FCSTD DOCUMENT  (FreeCAD 1.0RUnknown)
Label: wardrobe_drawer_jan_assy4
License: All rights reserved
objects: App::Link×7, App::DocumentObjectGroup×4, PartDesign::CoordinateSystem×1, App::FeaturePython×1, App::Part×1
note: 1 computed .brp shape members not serialized (recipe doc carries the construction recipe); baked Part::Feature solids carry a one-line shape summary decoded from their .brp
EXTERNAL_REF file=../purchased parts/hettich_rail_550mm.FCStd obj=LCS_left_center
EXTERNAL_REF file=../purchased parts/hettich_rail_550mm.FCStd obj=Body
EXTERNAL_REF file=parts/drawer_sides.FCStd obj=LCS_bottom_center
EXTERNAL_REF file=../purchased parts/hettich_rail_550mm.FCStd obj=LCS_inner_center
EXTERNAL_REF file=parts/drawer_sides.FCStd obj=Body
EXTERNAL_REF file=parts/drawer_front.FCStd obj=LCS_left
EXTERNAL_REF file=parts/drawer_sides.FCStd obj=LCS_1
EXTERNAL_REF file=parts/drawer_front.FCStd obj=Body
EXTERNAL_REF file=parts/drawer_front.FCStd obj=LCS_right
EXTERNAL_REF file=parts/drawer_sides.FCStd obj=LCS_2
EXTERNAL_REF file=parts/drawer_bottom.FCStd obj=LCS_front
EXTERNAL_REF file=parts/drawer_front.FCStd obj=LCS_bottom_center
EXTERNAL_REF file=parts/drawer_bottom.FCStd obj=Body
EXTERNAL_REF file=parts/drawer_back.FCStd obj=LCS_left
EXTERNAL_REF file=parts/drawer_back.FCStd obj=Body

FEATURE [App::DocumentObjectGroup] Parts
FEATURE [PartDesign::CoordinateSystem] LCS_Origin
  AttacherType = Attacher::AttachEngine3D
  AttachmentSupport = -> [X_Axis]
  MapMode = 2
FEATURE [App::DocumentObjectGroup] Constraints
FEATURE [App::FeaturePython] Variables  # WARN: FeaturePython — macro-defined, semantics opaque (R4)
  Type = App::PropertyContainer
FEATURE [App::DocumentObjectGroup] Configurations
FEATURE [App::Link] hettich_rail_550
  AttachedBy = #LCS_left_center
  AttachedTo = Parent Assembly#LCS_Origin
  LinkPlacement = pos=(17.5,-9e-16,-1.6e-14) rot=(-0.57735,-0.57735,-0.57735;2.0944rad)
  LinkedObject = -> <external ../purchased parts/hettich_rail_550mm.FCStd>#Body
  Placement = pos=(17.5,-9e-16,-1.6e-14) rot=(-0.57735,-0.57735,-0.57735;2.0944rad)
  SolverId = Asm4EE
  expr: Placement = LCS_Origin.Placement * AttachmentOffset * hettich_rail_550mm#LCS_left_center.Placement ^ -1
FEATURE [App::Link] drawer_sides
  AttachedBy = #LCS_bottom_center
  AttachedTo = hettich_rail_550#LCS_inner_center
  AttachmentOffset = pos=(0,0,0) rot=(0,0,1;4.71239rad)
  LinkPlacement = pos=(90,22,256) rot=(0.57735,0.57735,0.57735;2.0944rad)
  LinkedObject = -> <external parts/drawer_sides.FCStd>#Body
  Placement = pos=(90,22,256) rot=(0.57735,0.57735,0.57735;2.0944rad)
  SolverId = Asm4EE
  expr: Placement = hettich_rail_550.Placement * hettich_rail_550mm#LCS_inner_center.Placement * AttachmentOffset * drawer_sides#LCS_bottom_center.Placement ^ -1
FEATURE [App::Link] drawer_front
  AttachedBy = #LCS_left
  AttachedTo = drawer_sides#LCS_1
  AttachmentOffset = pos=(0,0,0) rot=(0.707107,-0.707107,0;3.14159rad)
  LinkPlacement = pos=(90,12.5,-265.5) rot=(-0.707107,0,-0.707107;3.14159rad)
  LinkedObject = -> <external parts/drawer_front.FCStd>#Body
  Placement = pos=(90,12.5,-265.5) rot=(-0.707107,0,-0.707107;3.14159rad)
  SolverId = Asm4EE
  expr: Placement = drawer_sides.Placement * drawer_sides#LCS_1.Placement * AttachmentOffset * drawer_front#LCS_left.Placement ^ -1
FEATURE [App::Link] drawer_sides001
  AttachedBy = #LCS_2
  AttachedTo = drawer_front#LCS_right
  AttachmentOffset = pos=(0,0,0) rot=(0.707107,0.707107,0;3.14159rad)
  LinkPlacement = pos=(90,480,-256) rot=(0.57735,-0.57735,0.57735;4.18879rad)
  LinkedObject = -> <external parts/drawer_sides.FCStd>#Body
  Placement = pos=(90,480,-256) rot=(0.57735,-0.57735,0.57735;4.18879rad)
  SolverId = Asm4EE
  expr: Placement = drawer_front.Placement * drawer_front#LCS_right.Placement * AttachmentOffset * drawer_sides#LCS_2.Placement ^ -1
FEATURE [App::Link] drawer_bottom
  AttachedBy = #LCS_front
  AttachedTo = drawer_front#LCS_bottom_center
  AttachmentOffset = pos=(0,0,0) rot=(0,1,0;3.14159rad)
  LinkPlacement = pos=(15,251,5.75) rot=(0.57735,0.57735,0.57735;2.0944rad)
  LinkedObject = -> <external parts/drawer_bottom.FCStd>#Body
  Placement = pos=(15,251,5.75) rot=(0.57735,0.57735,0.57735;2.0944rad)
  SolverId = Asm4EE
  expr: Placement = drawer_front.Placement * drawer_front#LCS_bottom_center.Placement * AttachmentOffset * drawer_bottom#LCS_front.Placement ^ -1
FEATURE [App::Link] drawer_back
  AttachedBy = #LCS_left
  AttachedTo = drawer_sides#LCS_2
  AttachmentOffset = pos=(0,0,0) rot=(0.707107,0.707107,0;3.14159rad)
  LinkPlacement = pos=(98.25,489.5,265.5) rot=(0,1,0;1.5708rad)
  LinkedObject = -> <external parts/drawer_back.FCStd>#Body
  Placement = pos=(98.25,489.5,265.5) rot=(0,1,0;1.5708rad)
  SolverId = Asm4EE
  expr: Placement = drawer_sides.Placement * drawer_sides#LCS_2.Placement * AttachmentOffset * drawer_back#LCS_left.Placement ^ -1
FEATURE [App::Link] hettich_rail_551
  AttachedBy = #LCS_inner_center
  AttachedTo = drawer_sides001#LCS_bottom_center
  AttachmentOffset = pos=(0,0,0) rot=(0,0,1;1.5708rad)
  LinkPlacement = pos=(17.5,502,9.73e-14) rot=(-0.57735,-0.57735,0.57735;4.18879rad)
  LinkedObject = -> <external ../purchased parts/hettich_rail_550mm.FCStd>#Body
  Placement = pos=(17.5,502,9.73e-14) rot=(-0.57735,-0.57735,0.57735;4.18879rad)
  SolverId = Asm4EE
  expr: Placement = drawer_sides001.Placement * drawer_sides#LCS_bottom_center.Placement * AttachmentOffset * hettich_rail_550mm#LCS_inner_center.Placement ^ -1
FEATURE [App::Part] Assembly  label="wardrobe_drawer_jan_assy4"
  AssemblyType = Part::Link
  Group = -> [LCS_Origin,Constraints,Variables,Configurations,hettich_rail_550,drawer_sides,drawer_front,drawer_sides001,drawer_bottom,drawer_back,hettich_rail_551]
  Origin = -> Origin
  Type = Assembly
FEATURE [App::DocumentObjectGroup] Group  label="Gruppe"

RESOLVED EXTERNAL PARTS (link-assembly join: the EXTERNAL_REF files above that resolve inside this repo's crawl, each included once):
---- part parts/drawer_back.FCStd = doc fcstd_10e94b67beff ----
FCSTD DOCUMENT  (FreeCAD 1.0RUnknown)
Label: drawer_back
License: All rights reserved
objects: PartDesign::CoordinateSystem×2, Sketcher::SketchObject×1, PartDesign::Pad×1, PartDesign::Body×1
note: 8 computed .brp shape members not serialized (recipe doc carries the construction recipe); baked Part::Feature solids carry a one-line shape summary decoded from their .brp
EXTERNAL_REF file=../../mastersketch.FCStd obj=Spreadsheet

FEATURE [Sketcher::SketchObject] Sketch
  ArcFitTolerance = 1e-06
  AttachmentSupport = -> [XZ_Plane]
  FullyConstrained = true
  MakeInternals = false
  MapMode = 5
  Placement = pos=(0,0,0) rot=(1,0,0;1.5708rad)
  expr: Constraints[10] = mastersketch#Spreadsheet.drawer_outer_thickness
  expr: Constraints[11] = mastersketch#Spreadsheet.drawer_height - (mastersketch#Spreadsheet.drawer_bottom_thickness + mastersketch#Spreadsheet.drawer_bottom_tol + mastersketch#Spreadsheet.drawer_slot_height)
  sketch-geometry (5):
    g0: LineSegment StartX=-9.5 StartY=-76.75 StartZ=0 EndX=9.5 EndY=-76.75 EndZ=0
    g1: LineSegment StartX=9.5 StartY=-76.75 StartZ=0 EndX=9.5 EndY=76.75 EndZ=0
    g2: LineSegment StartX=9.5 StartY=76.75 StartZ=0 EndX=-9.5 EndY=76.75 EndZ=0
    g3: LineSegment StartX=-9.5 StartY=76.75 StartZ=0 EndX=-9.5 EndY=-76.75 EndZ=0
    g4: GeomPoint [constr] X=0 Y=0 Z=0
  constraints (12):
    c: Coincident(g0,g1)
    c: Coincident(g1,g2)
    c: Coincident(g2,g3)
    c: Coincident(g3,g0)
    c: Horizontal(g0)
    c: Horizontal(g2)
    c: Vertical(g1)
    c: Vertical(g3)
    c: Symmetric(g2,g0,g4)
    c: Coincident(g4,g-1)
    c: DistanceX(g0,g0) = 19
    c: DistanceY(g1,g1) = 153.5
FEATURE [PartDesign::Pad] Pad
  Direction = (0,-1,2e-16)
  Length = 477
  Length2 = 10
  Placement = pos=(0,0,0) rot=(1,0,0;1.5708rad)
  Profile = -> Sketch
  ReferenceAxis = -> Sketch [N_Axis]
  Refine = true
  Suppressed = false
  Type = 0
  expr: Length = mastersketch#Spreadsheet.drawer_width
FEATURE [PartDesign::CoordinateSystem] LCS_left
  AttacherType = Attacher::AttachEngine3D
  AttachmentSupport = -> [Pad]
  MapMode = 7
  Placement = pos=(9.5,-477,76.75) rot=(0,1,0;3.14159rad)
FEATURE [PartDesign::CoordinateSystem] LCS_right
  AttacherType = Attacher::AttachEngine3D
  AttachmentSupport = -> [Pad]
  MapMode = 7
  Placement = pos=(9.5,0,76.75) rot=(0,1,0;3.14159rad)
FEATURE [PartDesign::Body] Body  label="drawer_back"
  AllowCompound = false
  Group = -> [Sketch,Pad,LCS_left,LCS_right]
  Origin = -> Origin
  Tip = -> Pad
---- part parts/drawer_bottom.FCStd = doc fcstd_674dae41beb6 ----
FCSTD DOCUMENT  (FreeCAD 1.0RUnknown)
Label: drawer_bottom
License: All rights reserved
objects: Sketcher::SketchObject×1, PartDesign::Pad×1, PartDesign::CoordinateSystem×1, PartDesign::Body×1
note: 7 computed .brp shape members not serialized (recipe doc carries the construction recipe); baked Part::Feature solids carry a one-line shape summary decoded from their .brp
EXTERNAL_REF file=../../mastersketch.FCStd obj=Spreadsheet

FEATURE [Sketcher::SketchObject] Sketch
  ArcFitTolerance = 1e-06
  AttachmentSupport = -> [XY_Plane]
  FullyConstrained = true
  MakeInternals = false
  MapMode = 5
  expr: Constraints[10] = mastersketch#Spreadsheet.drawer_width + 2 * (mastersketch#Spreadsheet.drawer_slot_depth + mastersketch#Spreadsheet.drawer_bottom_tol) - 2 * mastersketch#Spreadsheet.drawer_outer_thickness - 2
  expr: Constraints[11] = mastersketch#Spreadsheet.drawer_length + mastersketch#Spreadsheet.drawer_slot_depth + mastersketch#Spreadsheet.drawer_bottom_tol - mastersketch#Spreadsheet.drawer_outer_thickness
  sketch-geometry (5):
    g0: LineSegment StartX=-227 StartY=-269.75 StartZ=0 EndX=227 EndY=-269.75 EndZ=0
    g1: LineSegment StartX=227 StartY=-269.75 StartZ=0 EndX=227 EndY=269.75 EndZ=0
    g2: LineSegment StartX=227 StartY=269.75 StartZ=0 EndX=-227 EndY=269.75 EndZ=0
    g3: LineSegment StartX=-227 StartY=269.75 StartZ=0 EndX=-227 EndY=-269.75 EndZ=0
    g4: GeomPoint [constr] X=0 Y=0 Z=0
  constraints (12):
    c: Coincident(g0,g1)
    c: Coincident(g1,g2)
    c: Coincident(g2,g3)
    c: Coincident(g3,g0)
    c: Horizontal(g0)
    c: Horizontal(g2)
    c: Vertical(g1)
    c: Vertical(g3)
    c: Symmetric(g2,g0,g4)
    c: Coincident(g4,g-1)
    c: DistanceX(g0,g0) = 454
    c: DistanceY(g1,g1) = 539.5
FEATURE [PartDesign::Pad] Pad
  Direction = (0,0,1)
  Length = 6
  Length2 = 10
  Profile = -> Sketch
  ReferenceAxis = -> Sketch [N_Axis]
  Refine = true
  Suppressed = false
  Type = 0
  expr: Length = mastersketch#Spreadsheet.drawer_bottom_thickness
FEATURE [PartDesign::CoordinateSystem] LCS_front
  AttacherType = Attacher::AttachEngine3D
  AttachmentSupport = -> [Pad]
  MapMode = 45
  Placement = pos=(0,-269.75,0) rot=(0.57735,0.57735,0.57735;2.0944rad)
FEATURE [PartDesign::Body] Body  label="drawer_bottom"
  AllowCompound = false
  Group = -> [Sketch,Pad,LCS_front]
  Origin = -> Origin
  Tip = -> Pad
---- part parts/drawer_front.FCStd = doc fcstd_8f72376a405c ----
FCSTD DOCUMENT  (FreeCAD 1.0RUnknown)
Label: drawer_front
License: All rights reserved
objects: PartDesign::CoordinateSystem×3, Sketcher::SketchObject×1, PartDesign::Pad×1, PartDesign::Body×1
note: 9 computed .brp shape members not serialized (recipe doc carries the construction recipe); baked Part::Feature solids carry a one-line shape summary decoded from their .brp
EXTERNAL_REF file=../../mastersketch.FCStd obj=Spreadsheet

FEATURE [Sketcher::SketchObject] Sketch
  ArcFitTolerance = 1e-06
  AttachmentSupport = -> [XZ_Plane]
  FullyConstrained = true
  MakeInternals = false
  MapMode = 5
  Placement = pos=(0,0,0) rot=(1,0,0;1.5708rad)
  expr: Constraints[13] = mastersketch#Spreadsheet.drawer_outer_thickness
  expr: Constraints[19] = mastersketch#Spreadsheet.drawer_bottom_thickness + mastersketch#Spreadsheet.drawer_bottom_tol
  expr: Constraints[20] = mastersketch#Spreadsheet.drawer_slot_height
  expr: Constraints[21] = mastersketch#Spreadsheet.drawer_height
  expr: Constraints[22] = mastersketch#Spreadsheet.drawer_slot_depth
  sketch-geometry (9):
    g0: LineSegment StartX=-9.5 StartY=-85 StartZ=0 EndX=9.5 EndY=-85 EndZ=0
    g1: LineSegment StartX=9.5 StartY=-85 StartZ=0 EndX=9.5 EndY=-75 EndZ=0
    g2: LineSegment StartX=9.5 StartY=85 StartZ=0 EndX=-9.5 EndY=85 EndZ=0
    g3: LineSegment StartX=-9.5 StartY=85 StartZ=0 EndX=-9.5 EndY=-85 EndZ=0
    g4: GeomPoint [constr] X=0 Y=0 Z=0
    g5: LineSegment StartX=9.5 StartY=-68.5 StartZ=0 EndX=1.5 EndY=-68.5 EndZ=0
    g6: LineSegment StartX=1.5 StartY=-68.5 StartZ=0 EndX=1.5 EndY=-75 EndZ=0
    g7: LineSegment StartX=1.5 StartY=-75 StartZ=0 EndX=9.5 EndY=-75 EndZ=0
    g8: LineSegment StartX=9.5 StartY=-68.5 StartZ=0 EndX=9.5 EndY=85 EndZ=0
  constraints (23):
    c: Coincident(g0,g1)
    c: Coincident(g8,g2)
    c: Coincident(g2,g3)
    c: Coincident(g3,g0)
    c: Horizontal(g0)
    c: Vertical(g1)
    c: Symmetric(g2,g0,g4)
    c: Coincident(g4,g-1)
    c: Coincident(g5,g6)
    c: Coincident(g6,g7)
    c: Vertical(g6)
    c: Horizontal(g5)
    c: Horizontal(g7)
    c: DistanceX(g2,g2) = 19
    c: Parallel(g3,g8)
    c: Coincident(g5,g8)
    c: Coincident(g7,g1)
    c: Vertical(g5,g1)
    c: Symmetric(g2,g2,g-2)
    c: Distance(g5,g1) = 6.5
    c: Distance(g6,g0) = 10
    c: DistanceY(g3,g3) = 170
    c: DistanceX(g5,g5) = 8
FEATURE [PartDesign::Pad] Pad
  Direction = (0,-1,2e-16)
  Length = 477
  Length2 = 10
  Placement = pos=(0,0,0) rot=(1,0,0;1.5708rad)
  Profile = -> Sketch
  ReferenceAxis = -> Sketch [N_Axis]
  Refine = true
  Suppressed = false
  Type = 0
  expr: Length = mastersketch#Spreadsheet.drawer_width
FEATURE [PartDesign::CoordinateSystem] LCS_left
  AttacherType = Attacher::AttachEngine3D
  AttachmentSupport = -> [Pad]
  MapMode = 7
  Placement = pos=(9.5,0,85) rot=(0,1,0;3.14159rad)
FEATURE [PartDesign::CoordinateSystem] LCS_right
  AttacherType = Attacher::AttachEngine3D
  AttachmentSupport = -> [Pad]
  MapMode = 7
  Placement = pos=(9.5,-477,85) rot=(0,1,0;3.14159rad)
FEATURE [PartDesign::CoordinateSystem] LCS_bottom_center
  AttacherType = Attacher::AttachEngine3D
  AttachmentSupport = -> [Pad]
  MapMode = 45
  Placement = pos=(1.5,-238.5,-75) rot=(0,0.707107,0.707107;3.14159rad)
FEATURE [PartDesign::Body] Body  label="drawer_front"
  AllowCompound = false
  Group = -> [Sketch,Pad,LCS_left,LCS_right,LCS_bottom_center]
  Origin = -> Origin
  Tip = -> Pad
---- part parts/drawer_sides.FCStd = doc fcstd_b4c7660c6d1a ----
FCSTD DOCUMENT  (FreeCAD 1.0RUnknown)
Label: drawer_sides
License: All rights reserved
objects: PartDesign::CoordinateSystem×3, Sketcher::SketchObject×1, PartDesign::Pad×1, PartDesign::Body×1
note: 9 computed .brp shape members not serialized (recipe doc carries the construction recipe); baked Part::Feature solids carry a one-line shape summary decoded from their .brp
EXTERNAL_REF file=../../mastersketch.FCStd obj=Spreadsheet

FEATURE [Sketcher::SketchObject] Sketch
  ArcFitTolerance = 1e-06
  AttachmentSupport = -> [XZ_Plane]
  FullyConstrained = true
  MakeInternals = false
  MapMode = 5
  Placement = pos=(0,0,0) rot=(1,0,0;1.5708rad)
  expr: Constraints[13] = mastersketch#Spreadsheet.drawer_outer_thickness
  expr: Constraints[19] = mastersketch#Spreadsheet.drawer_bottom_thickness + mastersketch#Spreadsheet.drawer_bottom_tol
  expr: Constraints[20] = mastersketch#Spreadsheet.drawer_slot_height
  expr: Constraints[21] = mastersketch#Spreadsheet.drawer_height
  expr: Constraints[22] = mastersketch#Spreadsheet.drawer_slot_depth
  sketch-geometry (9):
    g0: LineSegment StartX=-9.5 StartY=-85 StartZ=0 EndX=9.5 EndY=-85 EndZ=0
    g1: LineSegment StartX=9.5 StartY=-85 StartZ=0 EndX=9.5 EndY=-75 EndZ=0
    g2: LineSegment StartX=9.5 StartY=85 StartZ=0 EndX=-9.5 EndY=85 EndZ=0
    g3: LineSegment StartX=-9.5 StartY=85 StartZ=0 EndX=-9.5 EndY=-85 EndZ=0
    g4: GeomPoint [constr] X=0 Y=0 Z=0
    g5: LineSegment StartX=9.5 StartY=-68.5 StartZ=0 EndX=1.5 EndY=-68.5 EndZ=0
    g6: LineSegment StartX=1.5 StartY=-68.5 StartZ=0 EndX=1.5 EndY=-75 EndZ=0
    g7: LineSegment StartX=1.5 StartY=-75 StartZ=0 EndX=9.5 EndY=-75 EndZ=0
    g8: LineSegment StartX=9.5 StartY=-68.5 StartZ=0 EndX=9.5 EndY=85 EndZ=0
  constraints (23):
    c: Coincident(g0,g1)
    c: Coincident(g8,g2)
    c: Coincident(g2,g3)
    c: Coincident(g3,g0)
    c: Horizontal(g0)
    c: Vertical(g1)
    c: Symmetric(g2,g0,g4)
    c: Coincident(g4,g-1)
    c: Coincident(g5,g6)
    c: Coincident(g6,g7)
    c: Vertical(g6)
    c: Horizontal(g5)
    c: Horizontal(g7)
    c: DistanceX(g2,g2) = 19
    c: Parallel(g3,g8)
    c: Coincident(g5,g8)
    c: Coincident(g7,g1)
    c: Vertical(g5,g1)
    c: Symmetric(g2,g2,g-2)
    c: Distance(g5,g1) = 6.5
    c: Distance(g6,g0) = 10
    c: DistanceY(g3,g3) = 170
    c: DistanceX(g5,g5) = 8
FEATURE [PartDesign::Pad] Pad
  Direction = (0,-1,2e-16)
  Length = 512
  Length2 = 10
  Placement = pos=(0,0,0) rot=(1,0,0;1.5708rad)
  Profile = -> Sketch
  ReferenceAxis = -> Sketch [N_Axis]
  Refine = true
  Suppressed = false
  Type = 0
  expr: Length = mastersketch#Spreadsheet.drawer_length - 2 * mastersketch#Spreadsheet.drawer_outer_thickness
FEATURE [PartDesign::CoordinateSystem] LCS_bottom_center
  AttacherType = Attacher::AttachEngine3D
  AttachmentSupport = -> [Pad]
  MapMode = 45
  Placement = pos=(-9.5,-256,-85) rot=(0,0.707107,0.707107;3.14159rad)
FEATURE [PartDesign::CoordinateSystem] LCS_1
  AttacherType = Attacher::AttachEngine3D
  AttachmentSupport = -> [Pad]
  MapMode = 7
  Placement = pos=(-9.5,-512,85) rot=(0,0,1;0rad)
FEATURE [PartDesign::CoordinateSystem] LCS_2
  AttacherType = Attacher::AttachEngine3D
  AttachmentSupport = -> [Pad]
  MapMode = 7
  Placement = pos=(-9.5,0,85) rot=(0,0,1;0rad)
FEATURE [PartDesign::Body] Body  label="drawer_sides"
  AllowCompound = false
  Group = -> [Sketch,Pad,LCS_bottom_center,LCS_1,LCS_2]
  Origin = -> Origin
  Tip = -> Pad
